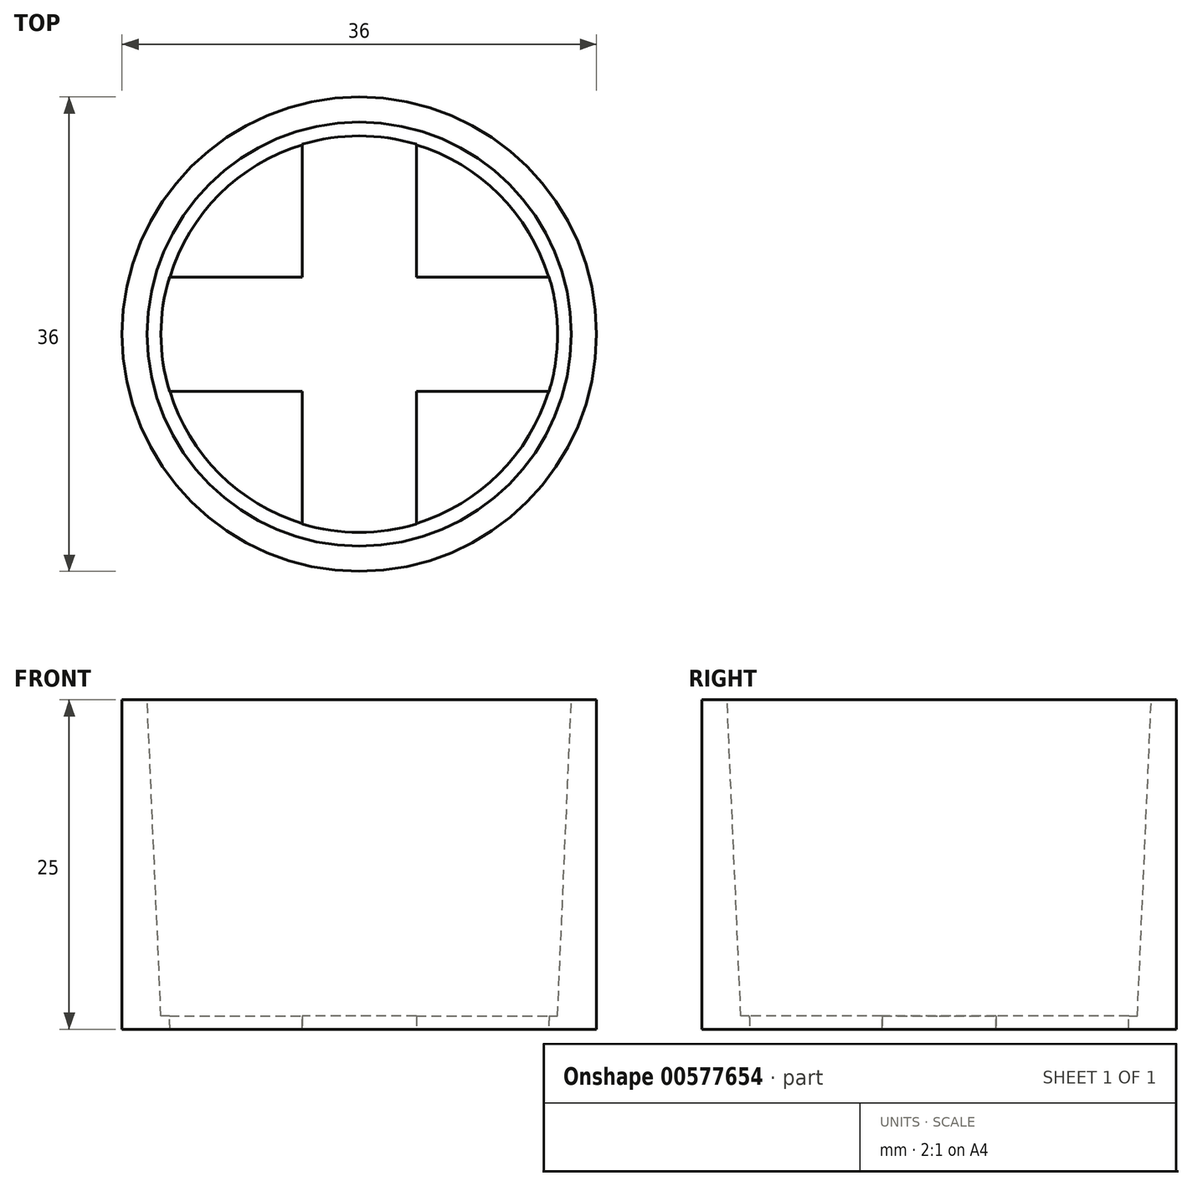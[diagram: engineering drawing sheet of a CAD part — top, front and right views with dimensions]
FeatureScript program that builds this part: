
annotation { "Feature Type Name" : "Feature", "Feature Type Description" : "" }
export const myFeature = defineFeature(function(context is Context, id is Id, definition is map)
    precondition{}
    {
        {
            var Q0;
            Q0=qCreatedBy(makeId("Top.planeOp"),FACE);
            var sketch = newSketch(context, id + "F0", { "sketchPlane" : qUnion([Q0])});
            skCircle(sketch, "E0", {"center": v(0, 0) * mm, "radius": 18 * mm});
            skCircle(sketch, "E1", {"center": v(0, 0) * mm, "radius": 15 * mm});
            skSolve(sketch);
        }
        {
            var Q0;
            Q0 = qSketchRegion(id + "F0", true);
            extrude(context, id + "F1", {"entities" : qUnion([Q0]), "depth" : 25 * mm, "offsetDistance" : 25 * mm});
        }
        {
            var Q0;
            Q0=makeQuery(id+"F1.opExtrude","CAP_EDGE",EDGE,{"disambiguationData":[OSD([sQuery(id+"F0.wireOp",EDGE,"E1")])],"isStart":false});
            chamfer(context, id + "F2", {"entities" : qUnion([Q0]), "chamferType" : ChamferType.OFFSET_ANGLE, "width" : 25 * mm, "oppositeDirection" : false, "angle" : 2.5 * degree, "tangentPropagation" : true});
        }
        {
            var Q0;
            Q0=qCreatedBy(makeId("Top.planeOp"),FACE);
            var sketch = newSketch(context, id + "F3", { "sketchPlane" : qUnion([Q0])});
            skLineSegment(sketch, "E2.bottom", {"start": v(4.33, 15.53) * mm, "end": v(-4.33, 15.53) * mm});
            skLineSegment(sketch, "E2.top", {"start": v(4.33, -15.53) * mm, "end": v(-4.33, -15.53) * mm});
            skLineSegment(sketch, "E2.left", {"start": v(4.33, 15.53) * mm, "end": v(4.33, -15.53) * mm});
            skLineSegment(sketch, "E2.right", {"start": v(-4.33, 15.53) * mm, "end": v(-4.33, -15.53) * mm});
            skPoint(sketch, "E2.middle", {"position": v(0, 0) * mm});
            skLineSegment(sketch, "E3.bottom", {"start": v(-15.53, 4.33) * mm, "end": v(-15.53, -4.33) * mm});
            skLineSegment(sketch, "E3.top", {"start": v(15.53, 4.33) * mm, "end": v(15.53, -4.33) * mm});
            skLineSegment(sketch, "E3.left", {"start": v(-15.53, 4.33) * mm, "end": v(15.53, 4.33) * mm});
            skLineSegment(sketch, "E3.right", {"start": v(-15.53, -4.33) * mm, "end": v(15.53, -4.33) * mm});
            skLineSegment(sketch, "E4.bottom", {"start": v(-15.53, -1.58) * mm, "end": v(15.53, -1.58) * mm});
            skLineSegment(sketch, "E4.top", {"start": v(-15.53, 1.58) * mm, "end": v(15.53, 1.58) * mm});
            skLineSegment(sketch, "E4.left", {"start": v(-15.53, -1.58) * mm, "end": v(-15.53, 1.58) * mm});
            skLineSegment(sketch, "E4.right", {"start": v(15.53, -1.58) * mm, "end": v(15.53, 1.58) * mm});
            skLineSegment(sketch, "E5.bottom", {"start": v(1.5, 15.53) * mm, "end": v(-1.5, 15.53) * mm});
            skLineSegment(sketch, "E5.top", {"start": v(1.5, -15.53) * mm, "end": v(-1.5, -15.53) * mm});
            skLineSegment(sketch, "E5.left", {"start": v(1.5, 15.53) * mm, "end": v(1.5, -15.53) * mm});
            skLineSegment(sketch, "E5.right", {"start": v(-1.5, 15.53) * mm, "end": v(-1.5, -15.53) * mm});
            skSolve(sketch);
        }
        {
            var Q0;
            {var subQ5=sQuery(id+"F3.wireOp",EDGE,"E3.bottom");Q0=makeQuery(id+"F3.imprint","IMPRINT",FACE,{"disambiguationData":[TD([[makeQuery(id+"F3.imprint","IMPRINT",EDGE,{"derivedFrom":subQ5}),1.0]])]});}
            var Q1;
            {var subQ0=sQuery(id+"F3.wireOp",EDGE,"E2.bottom");Q1=makeQuery(id+"F3.imprint","IMPRINT",FACE,{"disambiguationData":[TD([[makeQuery(id+"F3.imprint","IMPRINT",EDGE,{"derivedFrom":subQ0}),1.0]])]});}
            var Q2;
            {var subQ5=sQuery(id+"F3.wireOp",EDGE,"E3.top");Q2=makeQuery(id+"F3.imprint","IMPRINT",FACE,{"disambiguationData":[TD([[makeQuery(id+"F3.imprint","IMPRINT",EDGE,{"derivedFrom":subQ5}),-1.0]])]});}
            var Q3;
            {var subQ0=sQuery(id+"F3.wireOp",EDGE,"E2.top");Q3=makeQuery(id+"F3.imprint","IMPRINT",FACE,{"disambiguationData":[TD([[makeQuery(id+"F3.imprint","IMPRINT",EDGE,{"derivedFrom":subQ0}),-1.0]])]});}
            var Q4;
            {var subQ0=sQuery(id+"F3.wireOp",EDGE,"E3.left");var subQ1=sQuery(id+"F3.wireOp",EDGE,"E2.left");var subQ2=makeQuery(id+"F3.imprint","INTERSECT",VERTEX,{"derivedFrom":[subQ1,subQ0]});Q4=makeQuery(id+"F3.imprint","IMPRINT",FACE,{"disambiguationData":[TD([[makeQuery(id+"F3.imprint","IMPRINT",EDGE,{"disambiguationData":[TD([[subQ2,-1.0]])],"derivedFrom":subQ1}),-1.0]])]});}
            var Q5;
            {var subQ0=sQuery(id+"F3.wireOp",EDGE,"E3.left");var subQ1=sQuery(id+"F3.wireOp",EDGE,"E2.right");var subQ2=makeQuery(id+"F3.imprint","INTERSECT",VERTEX,{"derivedFrom":[subQ1,subQ0]});Q5=makeQuery(id+"F3.imprint","IMPRINT",FACE,{"disambiguationData":[TD([[makeQuery(id+"F3.imprint","IMPRINT",EDGE,{"disambiguationData":[TD([[subQ2,-1.0]])],"derivedFrom":subQ1}),1.0]])]});}
            var Q6;
            {var subQ0=sQuery(id+"F3.wireOp",EDGE,"E4.top");var subQ1=sQuery(id+"F3.wireOp",EDGE,"E2.right");var subQ2=makeQuery(id+"F3.imprint","INTERSECT",VERTEX,{"derivedFrom":[subQ1,subQ0]});Q6=makeQuery(id+"F3.imprint","IMPRINT",FACE,{"disambiguationData":[TD([[makeQuery(id+"F3.imprint","IMPRINT",EDGE,{"disambiguationData":[TD([[subQ2,-1.0]])],"derivedFrom":subQ1}),1.0]])]});}
            var Q7;
            {var subQ0=sQuery(id+"F3.wireOp",EDGE,"E3.right");var subQ1=sQuery(id+"F3.wireOp",EDGE,"E2.right");var subQ2=makeQuery(id+"F3.imprint","INTERSECT",VERTEX,{"derivedFrom":[subQ1,subQ0]});Q7=makeQuery(id+"F3.imprint","IMPRINT",FACE,{"disambiguationData":[TD([[makeQuery(id+"F3.imprint","IMPRINT",EDGE,{"disambiguationData":[TD([[subQ2,1.0]])],"derivedFrom":subQ1}),1.0]])]});}
            var Q8;
            {var subQ0=sQuery(id+"F3.wireOp",EDGE,"E5.right");var subQ1=sQuery(id+"F3.wireOp",EDGE,"E3.right");var subQ2=makeQuery(id+"F3.imprint","INTERSECT",VERTEX,{"derivedFrom":[subQ1,subQ0]});Q8=makeQuery(id+"F3.imprint","IMPRINT",FACE,{"disambiguationData":[TD([[makeQuery(id+"F3.imprint","IMPRINT",EDGE,{"disambiguationData":[TD([[subQ2,-1.0]])],"derivedFrom":subQ1}),1.0]])]});}
            var Q9;
            {var subQ0=sQuery(id+"F3.wireOp",EDGE,"E3.right");var subQ1=sQuery(id+"F3.wireOp",EDGE,"E2.left");var subQ2=makeQuery(id+"F3.imprint","INTERSECT",VERTEX,{"derivedFrom":[subQ1,subQ0]});Q9=makeQuery(id+"F3.imprint","IMPRINT",FACE,{"disambiguationData":[TD([[makeQuery(id+"F3.imprint","IMPRINT",EDGE,{"disambiguationData":[TD([[subQ2,1.0]])],"derivedFrom":subQ1}),-1.0]])]});}
            var Q10;
            {var subQ0=sQuery(id+"F3.wireOp",EDGE,"E4.top");var subQ1=sQuery(id+"F3.wireOp",EDGE,"E2.left");var subQ2=makeQuery(id+"F3.imprint","INTERSECT",VERTEX,{"derivedFrom":[subQ1,subQ0]});Q10=makeQuery(id+"F3.imprint","IMPRINT",FACE,{"disambiguationData":[TD([[makeQuery(id+"F3.imprint","IMPRINT",EDGE,{"disambiguationData":[TD([[subQ2,-1.0]])],"derivedFrom":subQ1}),-1.0]])]});}
            var Q11;
            {var subQ0=sQuery(id+"F3.wireOp",EDGE,"E5.right");var subQ1=sQuery(id+"F3.wireOp",EDGE,"E3.left");var subQ2=makeQuery(id+"F3.imprint","INTERSECT",VERTEX,{"derivedFrom":[subQ1,subQ0]});Q11=makeQuery(id+"F3.imprint","IMPRINT",FACE,{"disambiguationData":[TD([[makeQuery(id+"F3.imprint","IMPRINT",EDGE,{"disambiguationData":[TD([[subQ2,-1.0]])],"derivedFrom":subQ1}),-1.0]])]});}
            var Q12;
            {var subQ0=sQuery(id+"F3.wireOp",EDGE,"E5.right");var subQ1=sQuery(id+"F3.wireOp",EDGE,"E4.bottom");var subQ2=makeQuery(id+"F3.imprint","INTERSECT",VERTEX,{"derivedFrom":[subQ1,subQ0]});Q12=makeQuery(id+"F3.imprint","IMPRINT",FACE,{"disambiguationData":[TD([[makeQuery(id+"F3.imprint","IMPRINT",EDGE,{"disambiguationData":[TD([[subQ2,-1.0]])],"derivedFrom":subQ1}),1.0]])]});}
            extrude(context, id + "F4", {"entities" : qUnion([Q0, Q1, Q2, Q3, Q4, Q5, Q6, Q7, Q8, Q9, Q10, Q11, Q12]), "operationType" : NewBodyOperationType.ADD, "depth" : 1 * mm, "offsetDistance" : 25 * mm});
        }
    });
